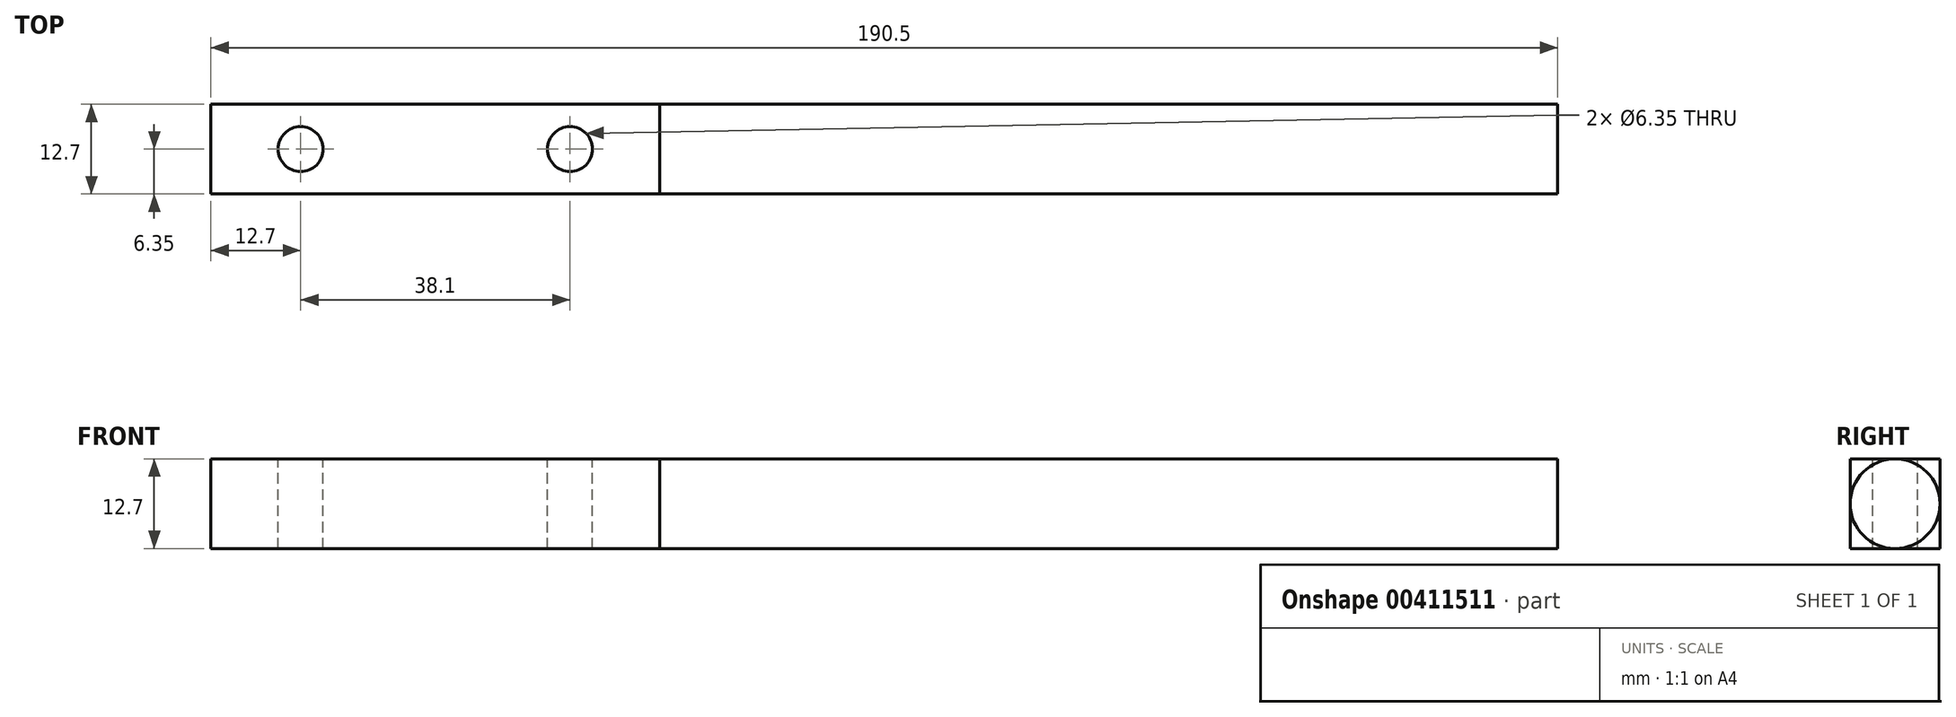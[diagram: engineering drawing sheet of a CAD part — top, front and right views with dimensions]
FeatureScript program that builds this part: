
annotation { "Feature Type Name" : "Feature", "Feature Type Description" : "" }
export const myFeature = defineFeature(function(context is Context, id is Id, definition is map)
    precondition{}
    {
        {
            var Q0;
            Q0=qCreatedBy(makeId("Right.planeOp"),FACE);
            var sketch = newSketch(context, id + "F0", { "sketchPlane" : qUnion([Q0])});
            skLineSegment(sketch, "E0.bottom", {"start": v(6.35, 6.35) * mm, "end": v(-6.35, 6.35) * mm});
            skLineSegment(sketch, "E0.top", {"start": v(6.35, -6.35) * mm, "end": v(-6.35, -6.35) * mm});
            skLineSegment(sketch, "E0.left", {"start": v(6.35, 6.35) * mm, "end": v(6.35, -6.35) * mm});
            skLineSegment(sketch, "E0.right", {"start": v(-6.35, 6.35) * mm, "end": v(-6.35, -6.35) * mm});
            skPoint(sketch, "E0.middle", {"position": v(0, 0) * mm});
            skSolve(sketch);
        }
        {
            var Q0;
            Q0=qSketchRegion(id+"F0",true);
            extrude(context, id + "F1", {"entities" : qUnion([Q0]), "depth" : 63.5 * mm});
        }
        {
            var Q0;
            Q0=makeQuery(id+"F1.opExtrude","CAP_FACE",FACE,{"disambiguationData":[OSD([sQuery(id+"F0.wireOp",EDGE,"E0.bottom"),sQuery(id+"F0.wireOp",EDGE,"E0.top"),sQuery(id+"F0.wireOp",EDGE,"E0.left"),sQuery(id+"F0.wireOp",EDGE,"E0.right")])],"isStart":false});
            var sketch = newSketch(context, id + "F2", { "sketchPlane" : qUnion([Q0])});
            skCircle(sketch, "E1", {"center": v(0, 0) * mm, "radius": 6.35 * mm});
            skSolve(sketch);
        }
        {
            var Q0;
            Q0=qSketchRegion(id+"F2",true);
            extrude(context, id + "F3", {"entities" : qUnion([Q0]), "operationType" : NewBodyOperationType.ADD, "depth" : 127 * mm});
        }
        {
            var Q0;
            Q0=makeQuery(id+"F1.opExtrude","SWEPT_FACE",FACE,{"disambiguationData":[OSD([sQuery(id+"F0.wireOp",EDGE,"E0.bottom")])]});
            var sketch = newSketch(context, id + "F4", { "sketchPlane" : qUnion([Q0])});
            skCircle(sketch, "E2", {"center": v(12.7, 0) * mm, "radius": 3.18 * mm});
            skCircle(sketch, "E3", {"center": v(50.8, 0) * mm, "radius": 3.18 * mm});
            skSolve(sketch);
        }
        {
            var Q0;
            Q0=sQuery(id+"F4.wireOp",VERTEX,"E2.center");
            var Q1;
            Q1=sQuery(id+"F4.wireOp",VERTEX,"E3.center");
            var Q2;
            Q2=makeQuery(id+"F1.opExtrude","SWEPT_BODY",BODY,{"disambiguationData":[OSD([sQuery(id+"F0.wireOp",EDGE,"E0.bottom"),sQuery(id+"F0.wireOp",EDGE,"E0.top"),sQuery(id+"F0.wireOp",EDGE,"E0.left"),sQuery(id+"F0.wireOp",EDGE,"E0.right")])]});
            hole(context, id + "F5", {"style" : HoleStyle.SIMPLE, "endStyle" : HoleEndStyle.THROUGH, "holeDiameter" : 6.35 * mm, "isTappedThrough" : true, "tappedDepth" : 12.7 * mm, "tapClearance" : 3, "locations" : qUnion([Q0, Q1]), "scope" : qUnion([Q2])});
        }
    });
